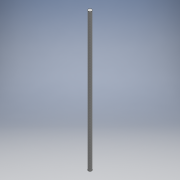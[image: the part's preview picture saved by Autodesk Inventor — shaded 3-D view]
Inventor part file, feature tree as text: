
AUTODESK INVENTOR PART (.ipt)
format: ipt  version: 2018 (Build 220112000, 112)  size: 92,160 bytes
history: native  units: mm
features: other x1, extrude x1, thread x1, sketch x1
ambient origin geometry x8: Origin, YZ Plane, XZ Plane, XY Plane, X Axis, Y Axis, Z Axis, Center Point
bodies: Body1 (feature_tree)
feature tree (4):
  other  "ソリッド1"
  extrude  "押し出し1"  Depth=10.0mm
  thread  "ねじ1"
  sketch  "スケッチ1"
